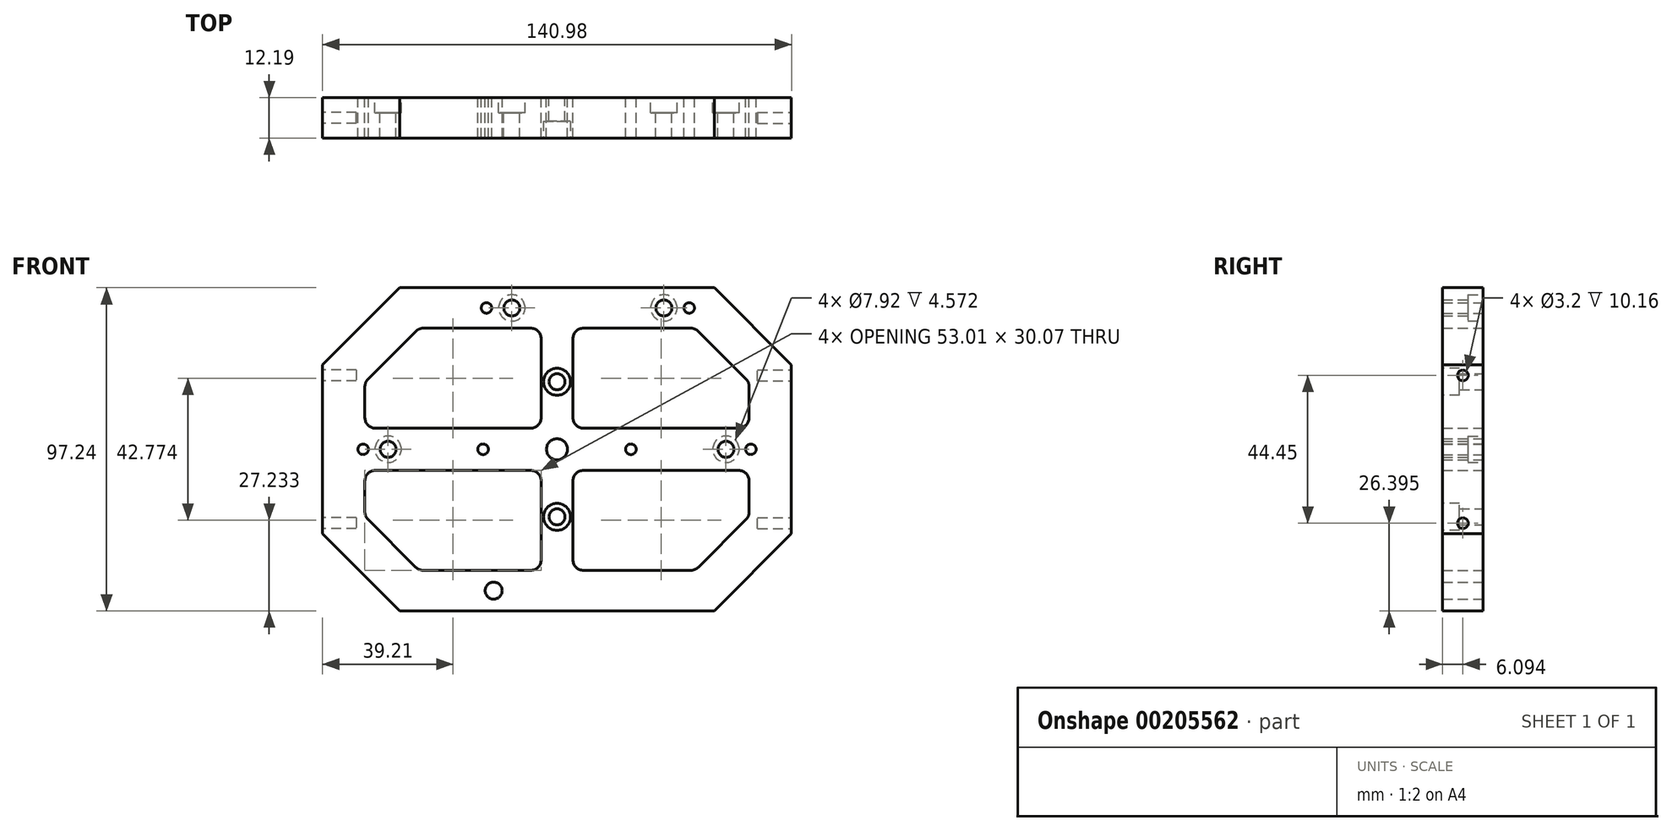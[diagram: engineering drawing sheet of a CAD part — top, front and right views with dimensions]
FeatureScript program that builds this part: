
annotation { "Feature Type Name" : "Feature", "Feature Type Description" : "" }
export const myFeature = defineFeature(function(context is Context, id is Id, definition is map)
    precondition{}
    {
        {
            var Q0;
            Q0=qCreatedBy(makeId("Front.planeOp"),FACE);
            var sketch = newSketch(context, id + "F0", { "sketchPlane" : qUnion([Q0])});
            skLineSegment(sketch, "E0", {"start": v(0, 48.62) * mm, "end": v(-47.27, 48.62) * mm});
            skLineSegment(sketch, "E1", {"start": v(-47.27, 48.62) * mm, "end": v(-70.49, 25.4) * mm});
            skLineSegment(sketch, "E2", {"start": v(-70.48, 25.4) * mm, "end": v(-70.48, 0) * mm});
            skLineSegment(sketch, "E3", {"start": v(-7.95, 36.42) * mm, "end": v(-40.19, 36.42) * mm});
            skLineSegment(sketch, "E4", {"start": v(-42.43, 35.5) * mm, "end": v(-56.86, 21.07) * mm});
            skLineSegment(sketch, "E5", {"start": v(-57.79, 18.82) * mm, "end": v(-57.79, 9.53) * mm});
            skLineSegment(sketch, "E6", {"start": v(-54.61, 6.35) * mm, "end": v(-7.95, 6.35) * mm});
            skLineSegment(sketch, "E7.MirrorCS", {"start": v(0, 48.62) * mm, "end": v(47.27, 48.62) * mm});
            skLineSegment(sketch, "E8.MirrorCS", {"start": v(70.48, 25.4) * mm, "end": v(70.48, 0) * mm});
            skLineSegment(sketch, "E9.MirrorCS", {"start": v(47.27, 48.62) * mm, "end": v(70.48, 25.4) * mm});
            skLineSegment(sketch, "E10.MirrorCS", {"start": v(-4.78, 9.53) * mm, "end": v(-4.78, 33.25) * mm});
            skLineSegment(sketch, "E11.MirrorCS", {"start": v(-70.48, -25.4) * mm, "end": v(-70.48, 0) * mm});
            skLineSegment(sketch, "E12.MirrorCS", {"start": v(-47.27, -48.62) * mm, "end": v(-70.48, -25.4) * mm});
            skLineSegment(sketch, "E13.MirrorCS", {"start": v(0, -48.62) * mm, "end": v(47.27, -48.62) * mm});
            skLineSegment(sketch, "E14.MirrorCS", {"start": v(47.27, -48.62) * mm, "end": v(70.48, -25.4) * mm});
            skLineSegment(sketch, "E15.MirrorCS", {"start": v(0, -48.62) * mm, "end": v(-47.27, -48.62) * mm});
            skLineSegment(sketch, "E16.MirrorCS", {"start": v(70.48, -25.4) * mm, "end": v(70.48, 0) * mm});
            skPoint(sketch, "E17.visualSharp", {"position": v(-4.78, 6.35) * mm});
            skArc(sketch, "E17.filletArc", {"start": v(-7.95, 6.35) * mm, "mid": v(-5.7, 7.28) * mm, "end": v(-4.78, 9.53) * mm});
            skPoint(sketch, "E18.visualSharp", {"position": v(-4.78, 36.42) * mm});
            skArc(sketch, "E18.filletArc", {"start": v(-4.78, 33.25) * mm, "mid": v(-5.7, 35.5) * mm, "end": v(-7.95, 36.42) * mm});
            skPoint(sketch, "E19.visualSharp", {"position": v(-41.5, 36.42) * mm});
            skArc(sketch, "E19.filletArc", {"start": v(-40.19, 36.42) * mm, "mid": v(-41.4, 36.18) * mm, "end": v(-42.43, 35.5) * mm});
            skPoint(sketch, "E20.visualSharp", {"position": v(-57.79, 20.14) * mm});
            skArc(sketch, "E20.filletArc", {"start": v(-56.86, 21.07) * mm, "mid": v(-57.54, 20.04) * mm, "end": v(-57.78, 18.82) * mm});
            skPoint(sketch, "E21.visualSharp", {"position": v(-57.79, 6.35) * mm});
            skArc(sketch, "E21.filletArc", {"start": v(-57.79, 9.53) * mm, "mid": v(-56.86, 7.28) * mm, "end": v(-54.61, 6.35) * mm});
            skLineSegment(sketch, "E22.MirrorCS", {"start": v(54.61, 6.35) * mm, "end": v(7.95, 6.35) * mm});
            skLineSegment(sketch, "E23.MirrorCS", {"start": v(57.79, 18.82) * mm, "end": v(57.79, 9.53) * mm});
            skPoint(sketch, "E24.MirrorP", {"position": v(57.79, 6.35) * mm});
            skArc(sketch, "E25.MirrorCS", {"start": v(56.86, 21.07) * mm, "mid": v(57.54, 20.04) * mm, "end": v(57.78, 18.82) * mm});
            skPoint(sketch, "E26.MirrorP", {"position": v(57.79, 20.14) * mm});
            skArc(sketch, "E27.MirrorCS", {"start": v(57.79, 9.53) * mm, "mid": v(56.86, 7.28) * mm, "end": v(54.61, 6.35) * mm});
            skLineSegment(sketch, "E28.MirrorCS", {"start": v(42.43, 35.5) * mm, "end": v(56.86, 21.07) * mm});
            skArc(sketch, "E29.MirrorCS", {"start": v(40.19, 36.42) * mm, "mid": v(41.4, 36.18) * mm, "end": v(42.43, 35.5) * mm});
            skArc(sketch, "E30.MirrorCS", {"start": v(4.78, 33.25) * mm, "mid": v(5.7, 35.5) * mm, "end": v(7.95, 36.42) * mm});
            skArc(sketch, "E31.MirrorCS", {"start": v(7.95, 6.35) * mm, "mid": v(5.7, 7.28) * mm, "end": v(4.78, 9.53) * mm});
            skLineSegment(sketch, "E32.MirrorCS", {"start": v(7.95, 36.42) * mm, "end": v(40.19, 36.42) * mm});
            skPoint(sketch, "E33.MirrorP", {"position": v(4.78, 6.35) * mm});
            skPoint(sketch, "E34.MirrorP", {"position": v(4.78, 36.42) * mm});
            skPoint(sketch, "E35.MirrorP", {"position": v(41.5, 36.42) * mm});
            skLineSegment(sketch, "E36.MirrorCS", {"start": v(4.78, 9.53) * mm, "end": v(4.78, 33.25) * mm});
            skArc(sketch, "E37.MirrorCS", {"start": v(56.86, -21.07) * mm, "mid": v(57.54, -20.04) * mm, "end": v(57.78, -18.82) * mm});
            skArc(sketch, "E38.MirrorCS", {"start": v(57.79, -9.53) * mm, "mid": v(56.86, -7.28) * mm, "end": v(54.61, -6.35) * mm});
            skLineSegment(sketch, "E39.MirrorCS", {"start": v(57.79, -18.82) * mm, "end": v(57.79, -9.53) * mm});
            skPoint(sketch, "E40.MirrorP", {"position": v(57.79, -6.35) * mm});
            skPoint(sketch, "E41.MirrorP", {"position": v(57.79, -20.14) * mm});
            skArc(sketch, "E42.MirrorCS", {"start": v(40.19, -36.42) * mm, "mid": v(41.4, -36.18) * mm, "end": v(42.43, -35.5) * mm});
            skArc(sketch, "E43.MirrorCS", {"start": v(4.78, -33.25) * mm, "mid": v(5.7, -35.5) * mm, "end": v(7.95, -36.42) * mm});
            skLineSegment(sketch, "E44.MirrorCS", {"start": v(7.95, -36.42) * mm, "end": v(40.19, -36.42) * mm});
            skPoint(sketch, "E45.MirrorP", {"position": v(4.78, -36.42) * mm});
            skArc(sketch, "E46.MirrorCS", {"start": v(7.95, -6.35) * mm, "mid": v(5.7, -7.28) * mm, "end": v(4.78, -9.53) * mm});
            skPoint(sketch, "E47.MirrorP", {"position": v(41.5, -36.42) * mm});
            skPoint(sketch, "E48.MirrorP", {"position": v(4.78, -6.35) * mm});
            skLineSegment(sketch, "E49.MirrorCS", {"start": v(4.78, -9.53) * mm, "end": v(4.78, -33.25) * mm});
            skLineSegment(sketch, "E50.MirrorCS", {"start": v(42.43, -35.5) * mm, "end": v(56.86, -21.07) * mm});
            skLineSegment(sketch, "E51.MirrorCS", {"start": v(54.61, -6.35) * mm, "end": v(7.95, -6.35) * mm});
            skArc(sketch, "E52.MirrorCS", {"start": v(-40.19, -36.42) * mm, "mid": v(-41.4, -36.18) * mm, "end": v(-42.43, -35.5) * mm});
            skPoint(sketch, "E53.MirrorP", {"position": v(-41.5, -36.42) * mm});
            skArc(sketch, "E54.MirrorCS", {"start": v(-56.86, -21.07) * mm, "mid": v(-57.54, -20.04) * mm, "end": v(-57.78, -18.82) * mm});
            skArc(sketch, "E55.MirrorCS", {"start": v(-57.79, -9.53) * mm, "mid": v(-56.86, -7.28) * mm, "end": v(-54.61, -6.35) * mm});
            skLineSegment(sketch, "E56.MirrorCS", {"start": v(-57.79, -18.82) * mm, "end": v(-57.79, -9.53) * mm});
            skPoint(sketch, "E57.MirrorP", {"position": v(-57.79, -6.35) * mm});
            skLineSegment(sketch, "E58.MirrorCS", {"start": v(-42.43, -35.5) * mm, "end": v(-56.86, -21.07) * mm});
            skPoint(sketch, "E59.MirrorP", {"position": v(-57.79, -20.14) * mm});
            skArc(sketch, "E60.MirrorCS", {"start": v(-4.78, -33.25) * mm, "mid": v(-5.7, -35.5) * mm, "end": v(-7.95, -36.42) * mm});
            skArc(sketch, "E61.MirrorCS", {"start": v(-7.95, -6.35) * mm, "mid": v(-5.7, -7.28) * mm, "end": v(-4.78, -9.53) * mm});
            skPoint(sketch, "E62.MirrorP", {"position": v(-4.78, -36.42) * mm});
            skLineSegment(sketch, "E63.MirrorCS", {"start": v(-7.95, -36.42) * mm, "end": v(-40.19, -36.42) * mm});
            skPoint(sketch, "E64.MirrorP", {"position": v(-4.78, -6.35) * mm});
            skLineSegment(sketch, "E65.MirrorCS", {"start": v(-4.78, -9.53) * mm, "end": v(-4.78, -33.25) * mm});
            skLineSegment(sketch, "E66.MirrorCS", {"start": v(-54.61, -6.35) * mm, "end": v(-7.95, -6.35) * mm});
            skCircle(sketch, "E67", {"center": v(0, 0) * mm, "radius": 3.18 * mm});
            skCircle(sketch, "E68", {"center": v(-13.59, 42.52) * mm, "radius": 2.41 * mm});
            skCircle(sketch, "E69", {"center": v(-21.2, 42.52) * mm, "radius": 1.59 * mm});
            skCircle(sketch, "E70", {"center": v(32.13, 42.52) * mm, "radius": 2.41 * mm});
            skCircle(sketch, "E71", {"center": v(39.75, 42.52) * mm, "radius": 1.59 * mm});
            skCircle(sketch, "E72", {"center": v(58.3, 0) * mm, "radius": 1.59 * mm});
            skCircle(sketch, "E73", {"center": v(50.8, 0) * mm, "radius": 2.41 * mm});
            skCircle(sketch, "E74", {"center": v(-50.8, 0) * mm, "radius": 2.41 * mm});
            skCircle(sketch, "E75", {"center": v(-58.3, 0) * mm, "radius": 1.59 * mm});
            skCircle(sketch, "E76", {"center": v(-19.05, -42.52) * mm, "radius": 2.55 * mm});
            skSolve(sketch);
        }
        {
            var Q0;
            Q0=qSketchRegion(id+"F0",true);
            extrude(context, id + "F1", {"entities" : qUnion([Q0]), "depth" : 12.2 * mm});
        }
        {
            var Q0;
            Q0=makeQuery(id+"F1.opExtrude","CAP_FACE",FACE,{"disambiguationData":[OSD([sQuery(id+"F0.wireOp",EDGE,"E8.MirrorCS"),sQuery(id+"F0.wireOp",EDGE,"E1"),sQuery(id+"F0.wireOp",EDGE,"E4"),sQuery(id+"F0.wireOp",EDGE,"E2"),sQuery(id+"F0.wireOp",EDGE,"E6"),sQuery(id+"F0.wireOp",EDGE,"E5"),sQuery(id+"F0.wireOp",EDGE,"E0"),sQuery(id+"F0.wireOp",EDGE,"E9.MirrorCS"),sQuery(id+"F0.wireOp",EDGE,"E7.MirrorCS"),sQuery(id+"F0.wireOp",EDGE,"E12.MirrorCS"),sQuery(id+"F0.wireOp",EDGE,"E11.MirrorCS"),sQuery(id+"F0.wireOp",EDGE,"E14.MirrorCS"),sQuery(id+"F0.wireOp",EDGE,"E16.MirrorCS"),sQuery(id+"F0.wireOp",EDGE,"E13.MirrorCS"),sQuery(id+"F0.wireOp",EDGE,"E15.MirrorCS"),sQuery(id+"F0.wireOp",EDGE,"E20.filletArc"),sQuery(id+"F0.wireOp",EDGE,"E21.filletArc"),sQuery(id+"F0.wireOp",EDGE,"E22.MirrorCS"),sQuery(id+"F0.wireOp",EDGE,"E23.MirrorCS"),sQuery(id+"F0.wireOp",EDGE,"E25.MirrorCS"),sQuery(id+"F0.wireOp",EDGE,"E27.MirrorCS"),sQuery(id+"F0.wireOp",EDGE,"E28.MirrorCS"),sQuery(id+"F0.wireOp",EDGE,"E17.filletArc"),sQuery(id+"F0.wireOp",EDGE,"E18.filletArc"),sQuery(id+"F0.wireOp",EDGE,"E31.MirrorCS"),sQuery(id+"F0.wireOp",EDGE,"E19.filletArc"),sQuery(id+"F0.wireOp",EDGE,"E36.MirrorCS"),sQuery(id+"F0.wireOp",EDGE,"E10.MirrorCS"),sQuery(id+"F0.wireOp",EDGE,"E3"),sQuery(id+"F0.wireOp",EDGE,"E29.MirrorCS"),sQuery(id+"F0.wireOp",EDGE,"E30.MirrorCS"),sQuery(id+"F0.wireOp",EDGE,"E32.MirrorCS"),sQuery(id+"F0.wireOp",EDGE,"E37.MirrorCS"),sQuery(id+"F0.wireOp",EDGE,"E38.MirrorCS"),sQuery(id+"F0.wireOp",EDGE,"E39.MirrorCS"),sQuery(id+"F0.wireOp",EDGE,"E42.MirrorCS"),sQuery(id+"F0.wireOp",EDGE,"E43.MirrorCS"),sQuery(id+"F0.wireOp",EDGE,"E46.MirrorCS"),sQuery(id+"F0.wireOp",EDGE,"E44.MirrorCS"),sQuery(id+"F0.wireOp",EDGE,"E50.MirrorCS"),sQuery(id+"F0.wireOp",EDGE,"E49.MirrorCS"),sQuery(id+"F0.wireOp",EDGE,"E51.MirrorCS"),sQuery(id+"F0.wireOp",EDGE,"E52.MirrorCS"),sQuery(id+"F0.wireOp",EDGE,"E54.MirrorCS"),sQuery(id+"F0.wireOp",EDGE,"E55.MirrorCS"),sQuery(id+"F0.wireOp",EDGE,"E58.MirrorCS"),sQuery(id+"F0.wireOp",EDGE,"E56.MirrorCS"),sQuery(id+"F0.wireOp",EDGE,"E60.MirrorCS"),sQuery(id+"F0.wireOp",EDGE,"E61.MirrorCS"),sQuery(id+"F0.wireOp",EDGE,"E63.MirrorCS"),sQuery(id+"F0.wireOp",EDGE,"E66.MirrorCS"),sQuery(id+"F0.wireOp",EDGE,"E65.MirrorCS"),sQuery(id+"F0.wireOp",EDGE,"E67"),sQuery(id+"F0.wireOp",EDGE,"E68"),sQuery(id+"F0.wireOp",EDGE,"E69"),sQuery(id+"F0.wireOp",EDGE,"E70"),sQuery(id+"F0.wireOp",EDGE,"E71"),sQuery(id+"F0.wireOp",EDGE,"E72"),sQuery(id+"F0.wireOp",EDGE,"E73"),sQuery(id+"F0.wireOp",EDGE,"E74"),sQuery(id+"F0.wireOp",EDGE,"E75"),sQuery(id+"F0.wireOp",EDGE,"E76")])],"isStart":true});
            var sketch = newSketch(context, id + "F2", { "sketchPlane" : qUnion([Q0])});
            skCircle(sketch, "E77", {"center": v(50.8, 0) * mm, "radius": 3.96 * mm});
            skCircle(sketch, "E78", {"center": v(13.59, 42.52) * mm, "radius": 3.96 * mm});
            skCircle(sketch, "E79", {"center": v(-32.13, 42.52) * mm, "radius": 3.96 * mm});
            skCircle(sketch, "E80", {"center": v(-50.8, 0) * mm, "radius": 3.96 * mm});
            skSolve(sketch);
        }
        {
            var Q0;
            Q0=qSketchRegion(id+"F2",true);
            extrude(context, id + "F3", {"entities" : qUnion([Q0]), "operationType" : NewBodyOperationType.REMOVE, "oppositeDirection" : true, "depth" : 4.57 * mm});
        }
        {
            var Q0;
            Q0=makeQuery(id+"F1.opExtrude","SWEPT_FACE",FACE,{"disambiguationData":[OSD([sQuery(id+"F0.wireOp",EDGE,"E8.MirrorCS"),sQuery(id+"F0.wireOp",EDGE,"E16.MirrorCS")])]});
            var sketch = newSketch(context, id + "F4", { "sketchPlane" : qUnion([Q0])});
            skCircle(sketch, "E81", {"center": v(-6.1, 22.23) * mm, "radius": 1.6 * mm});
            skCircle(sketch, "E82", {"center": v(-6.1, -22.23) * mm, "radius": 1.6 * mm});
            skSolve(sketch);
        }
        {
            var Q0;
            Q0=qSketchRegion(id+"F4",true);
            extrude(context, id + "F5", {"entities" : qUnion([Q0]), "operationType" : NewBodyOperationType.REMOVE, "oppositeDirection" : true, "depth" : 10.16 * mm});
        }
        {
            var Q0;
            Q0=makeQuery(id+"F1.opExtrude","SWEPT_FACE",FACE,{"disambiguationData":[OSD([sQuery(id+"F0.wireOp",EDGE,"E2"),sQuery(id+"F0.wireOp",EDGE,"E11.MirrorCS")])]});
            var sketch = newSketch(context, id + "F6", { "sketchPlane" : qUnion([Q0])});
            skCircle(sketch, "E83", {"center": v(6.1, 22.23) * mm, "radius": 1.6 * mm});
            skCircle(sketch, "E84", {"center": v(6.1, -22.23) * mm, "radius": 1.6 * mm});
            skSolve(sketch);
        }
        {
            var Q0;
            Q0=qSketchRegion(id+"F6",true);
            extrude(context, id + "F7", {"entities" : qUnion([Q0]), "operationType" : NewBodyOperationType.REMOVE, "oppositeDirection" : true, "depth" : 10.16 * mm});
        }
        {
            var Q0;
            Q0=makeQuery(id+"F1.opExtrude","CAP_FACE",FACE,{"disambiguationData":[OSD([sQuery(id+"F0.wireOp",EDGE,"E8.MirrorCS"),sQuery(id+"F0.wireOp",EDGE,"E1"),sQuery(id+"F0.wireOp",EDGE,"E4"),sQuery(id+"F0.wireOp",EDGE,"E2"),sQuery(id+"F0.wireOp",EDGE,"E6"),sQuery(id+"F0.wireOp",EDGE,"E5"),sQuery(id+"F0.wireOp",EDGE,"E0"),sQuery(id+"F0.wireOp",EDGE,"E9.MirrorCS"),sQuery(id+"F0.wireOp",EDGE,"E7.MirrorCS"),sQuery(id+"F0.wireOp",EDGE,"E12.MirrorCS"),sQuery(id+"F0.wireOp",EDGE,"E11.MirrorCS"),sQuery(id+"F0.wireOp",EDGE,"E14.MirrorCS"),sQuery(id+"F0.wireOp",EDGE,"E16.MirrorCS"),sQuery(id+"F0.wireOp",EDGE,"E13.MirrorCS"),sQuery(id+"F0.wireOp",EDGE,"E15.MirrorCS"),sQuery(id+"F0.wireOp",EDGE,"E20.filletArc"),sQuery(id+"F0.wireOp",EDGE,"E21.filletArc"),sQuery(id+"F0.wireOp",EDGE,"E22.MirrorCS"),sQuery(id+"F0.wireOp",EDGE,"E23.MirrorCS"),sQuery(id+"F0.wireOp",EDGE,"E25.MirrorCS"),sQuery(id+"F0.wireOp",EDGE,"E27.MirrorCS"),sQuery(id+"F0.wireOp",EDGE,"E28.MirrorCS"),sQuery(id+"F0.wireOp",EDGE,"E17.filletArc"),sQuery(id+"F0.wireOp",EDGE,"E18.filletArc"),sQuery(id+"F0.wireOp",EDGE,"E31.MirrorCS"),sQuery(id+"F0.wireOp",EDGE,"E19.filletArc"),sQuery(id+"F0.wireOp",EDGE,"E36.MirrorCS"),sQuery(id+"F0.wireOp",EDGE,"E10.MirrorCS"),sQuery(id+"F0.wireOp",EDGE,"E3"),sQuery(id+"F0.wireOp",EDGE,"E29.MirrorCS"),sQuery(id+"F0.wireOp",EDGE,"E30.MirrorCS"),sQuery(id+"F0.wireOp",EDGE,"E32.MirrorCS"),sQuery(id+"F0.wireOp",EDGE,"E37.MirrorCS"),sQuery(id+"F0.wireOp",EDGE,"E38.MirrorCS"),sQuery(id+"F0.wireOp",EDGE,"E39.MirrorCS"),sQuery(id+"F0.wireOp",EDGE,"E42.MirrorCS"),sQuery(id+"F0.wireOp",EDGE,"E43.MirrorCS"),sQuery(id+"F0.wireOp",EDGE,"E46.MirrorCS"),sQuery(id+"F0.wireOp",EDGE,"E44.MirrorCS"),sQuery(id+"F0.wireOp",EDGE,"E50.MirrorCS"),sQuery(id+"F0.wireOp",EDGE,"E49.MirrorCS"),sQuery(id+"F0.wireOp",EDGE,"E51.MirrorCS"),sQuery(id+"F0.wireOp",EDGE,"E52.MirrorCS"),sQuery(id+"F0.wireOp",EDGE,"E54.MirrorCS"),sQuery(id+"F0.wireOp",EDGE,"E55.MirrorCS"),sQuery(id+"F0.wireOp",EDGE,"E58.MirrorCS"),sQuery(id+"F0.wireOp",EDGE,"E56.MirrorCS"),sQuery(id+"F0.wireOp",EDGE,"E60.MirrorCS"),sQuery(id+"F0.wireOp",EDGE,"E61.MirrorCS"),sQuery(id+"F0.wireOp",EDGE,"E63.MirrorCS"),sQuery(id+"F0.wireOp",EDGE,"E66.MirrorCS"),sQuery(id+"F0.wireOp",EDGE,"E65.MirrorCS"),sQuery(id+"F0.wireOp",EDGE,"E67"),sQuery(id+"F0.wireOp",EDGE,"E68"),sQuery(id+"F0.wireOp",EDGE,"E69"),sQuery(id+"F0.wireOp",EDGE,"E70"),sQuery(id+"F0.wireOp",EDGE,"E71"),sQuery(id+"F0.wireOp",EDGE,"E72"),sQuery(id+"F0.wireOp",EDGE,"E73"),sQuery(id+"F0.wireOp",EDGE,"E74"),sQuery(id+"F0.wireOp",EDGE,"E75"),sQuery(id+"F0.wireOp",EDGE,"E76")])],"isStart":true});
            var sketch = newSketch(context, id + "F8", { "sketchPlane" : qUnion([Q0])});
            skCircle(sketch, "E85", {"center": v(0, -20.32) * mm, "radius": 2.41 * mm});
            skCircle(sketch, "E86", {"center": v(0, 20.32) * mm, "radius": 2.41 * mm});
            skCircle(sketch, "E87", {"center": v(22.23, 0) * mm, "radius": 1.6 * mm});
            skCircle(sketch, "E88", {"center": v(-22.23, 0) * mm, "radius": 1.6 * mm});
            skSolve(sketch);
        }
        {
            var Q0;
            Q0=qSketchRegion(id+"F8",true);
            extrude(context, id + "F9", {"entities" : qUnion([Q0]), "operationType" : NewBodyOperationType.REMOVE, "endBound" : BoundingType.THROUGH_ALL, "oppositeDirection" : true, "depth" : 25.4 * mm});
        }
        {
            var Q0;
            Q0=makeQuery(id+"F1.opExtrude","CAP_FACE",FACE,{"disambiguationData":[OSD([sQuery(id+"F0.wireOp",EDGE,"E8.MirrorCS"),sQuery(id+"F0.wireOp",EDGE,"E1"),sQuery(id+"F0.wireOp",EDGE,"E4"),sQuery(id+"F0.wireOp",EDGE,"E2"),sQuery(id+"F0.wireOp",EDGE,"E6"),sQuery(id+"F0.wireOp",EDGE,"E5"),sQuery(id+"F0.wireOp",EDGE,"E0"),sQuery(id+"F0.wireOp",EDGE,"E9.MirrorCS"),sQuery(id+"F0.wireOp",EDGE,"E7.MirrorCS"),sQuery(id+"F0.wireOp",EDGE,"E12.MirrorCS"),sQuery(id+"F0.wireOp",EDGE,"E11.MirrorCS"),sQuery(id+"F0.wireOp",EDGE,"E14.MirrorCS"),sQuery(id+"F0.wireOp",EDGE,"E16.MirrorCS"),sQuery(id+"F0.wireOp",EDGE,"E13.MirrorCS"),sQuery(id+"F0.wireOp",EDGE,"E15.MirrorCS"),sQuery(id+"F0.wireOp",EDGE,"E20.filletArc"),sQuery(id+"F0.wireOp",EDGE,"E21.filletArc"),sQuery(id+"F0.wireOp",EDGE,"E22.MirrorCS"),sQuery(id+"F0.wireOp",EDGE,"E23.MirrorCS"),sQuery(id+"F0.wireOp",EDGE,"E25.MirrorCS"),sQuery(id+"F0.wireOp",EDGE,"E27.MirrorCS"),sQuery(id+"F0.wireOp",EDGE,"E28.MirrorCS"),sQuery(id+"F0.wireOp",EDGE,"E17.filletArc"),sQuery(id+"F0.wireOp",EDGE,"E18.filletArc"),sQuery(id+"F0.wireOp",EDGE,"E31.MirrorCS"),sQuery(id+"F0.wireOp",EDGE,"E19.filletArc"),sQuery(id+"F0.wireOp",EDGE,"E36.MirrorCS"),sQuery(id+"F0.wireOp",EDGE,"E10.MirrorCS"),sQuery(id+"F0.wireOp",EDGE,"E3"),sQuery(id+"F0.wireOp",EDGE,"E29.MirrorCS"),sQuery(id+"F0.wireOp",EDGE,"E30.MirrorCS"),sQuery(id+"F0.wireOp",EDGE,"E32.MirrorCS"),sQuery(id+"F0.wireOp",EDGE,"E37.MirrorCS"),sQuery(id+"F0.wireOp",EDGE,"E38.MirrorCS"),sQuery(id+"F0.wireOp",EDGE,"E39.MirrorCS"),sQuery(id+"F0.wireOp",EDGE,"E42.MirrorCS"),sQuery(id+"F0.wireOp",EDGE,"E43.MirrorCS"),sQuery(id+"F0.wireOp",EDGE,"E46.MirrorCS"),sQuery(id+"F0.wireOp",EDGE,"E44.MirrorCS"),sQuery(id+"F0.wireOp",EDGE,"E50.MirrorCS"),sQuery(id+"F0.wireOp",EDGE,"E49.MirrorCS"),sQuery(id+"F0.wireOp",EDGE,"E51.MirrorCS"),sQuery(id+"F0.wireOp",EDGE,"E52.MirrorCS"),sQuery(id+"F0.wireOp",EDGE,"E54.MirrorCS"),sQuery(id+"F0.wireOp",EDGE,"E55.MirrorCS"),sQuery(id+"F0.wireOp",EDGE,"E58.MirrorCS"),sQuery(id+"F0.wireOp",EDGE,"E56.MirrorCS"),sQuery(id+"F0.wireOp",EDGE,"E60.MirrorCS"),sQuery(id+"F0.wireOp",EDGE,"E61.MirrorCS"),sQuery(id+"F0.wireOp",EDGE,"E63.MirrorCS"),sQuery(id+"F0.wireOp",EDGE,"E66.MirrorCS"),sQuery(id+"F0.wireOp",EDGE,"E65.MirrorCS"),sQuery(id+"F0.wireOp",EDGE,"E67"),sQuery(id+"F0.wireOp",EDGE,"E68"),sQuery(id+"F0.wireOp",EDGE,"E69"),sQuery(id+"F0.wireOp",EDGE,"E70"),sQuery(id+"F0.wireOp",EDGE,"E71"),sQuery(id+"F0.wireOp",EDGE,"E72"),sQuery(id+"F0.wireOp",EDGE,"E73"),sQuery(id+"F0.wireOp",EDGE,"E74"),sQuery(id+"F0.wireOp",EDGE,"E75"),sQuery(id+"F0.wireOp",EDGE,"E76")])],"isStart":false});
            var sketch = newSketch(context, id + "F10", { "sketchPlane" : qUnion([Q0])});
            skCircle(sketch, "E89", {"center": v(0, -20.32) * mm, "radius": 4.06 * mm});
            skCircle(sketch, "E90", {"center": v(0, 20.32) * mm, "radius": 4.06 * mm});
            skSolve(sketch);
        }
        {
            var Q0;
            Q0=qSketchRegion(id+"F10",true);
            extrude(context, id + "F11", {"entities" : qUnion([Q0]), "operationType" : NewBodyOperationType.REMOVE, "oppositeDirection" : true, "depth" : 5.08 * mm});
        }
    });
